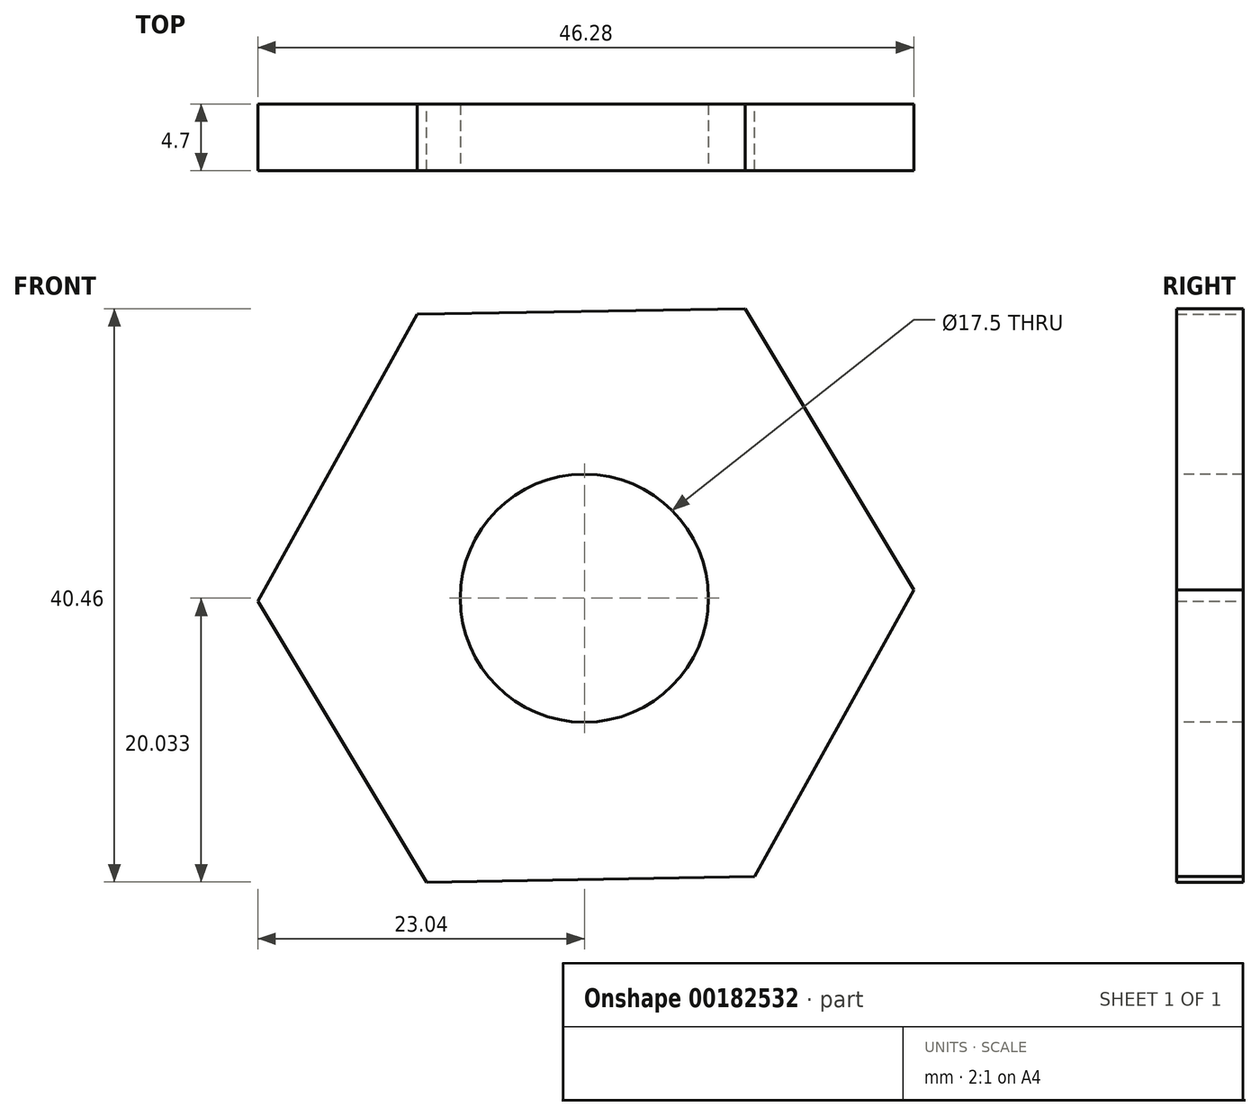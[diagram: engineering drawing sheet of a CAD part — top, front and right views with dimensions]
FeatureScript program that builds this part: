
annotation { "Feature Type Name" : "Feature", "Feature Type Description" : "" }
export const myFeature = defineFeature(function(context is Context, id is Id, definition is map)
    precondition{}
    {
        {
            var Q0;
            Q0=qCreatedBy(makeId("Front.planeOp"),FACE);
            var sketch = newSketch(context, id + "F0", { "sketchPlane" : qUnion([Q0])});
            skCircle(sketch, "E0.cCircle", {"center": v(-18.76, 37.82) * mm, "radius": 23.14 * mm, "construction": true});
            skLineSegment(sketch, "E0.0", {"start": v(4.38, 38.2) * mm, "end": v(-6.85, 17.97) * mm});
            skLineSegment(sketch, "E0.1", {"start": v(-6.85, 17.97) * mm, "end": v(-30, 17.59) * mm});
            skLineSegment(sketch, "E0.2", {"start": v(-30, 17.59) * mm, "end": v(-41.9, 37.43) * mm});
            skLineSegment(sketch, "E0.3", {"start": v(-41.9, 37.43) * mm, "end": v(-30.66, 57.66) * mm});
            skLineSegment(sketch, "E0.4", {"start": v(-30.66, 57.66) * mm, "end": v(-7.53, 58.05) * mm});
            skLineSegment(sketch, "E0.5", {"start": v(-7.53, 58.05) * mm, "end": v(4.38, 38.2) * mm});
            skSolve(sketch);
        }
        {
            var Q0;
            Q0=makeQuery(id+"F0.imprint","IMPRINT",FACE,{"disambiguationData":[TD([[makeQuery(id+"F0.imprint","IMPRINT",EDGE,{"derivedFrom":sQuery(id+"F0.wireOp",EDGE,"E0.0")}),-1.0]])]});
            extrude(context, id + "F1", {"entities" : qUnion([Q0]), "depth" : 4.7 * mm});
        }
        {
            var Q0;
            Q0=makeQuery(id+"F1.opExtrude","CAP_FACE",FACE,{"disambiguationData":[OSD([sQuery(id+"F0.wireOp",EDGE,"E0.0"),sQuery(id+"F0.wireOp",EDGE,"E0.1"),sQuery(id+"F0.wireOp",EDGE,"E0.2"),sQuery(id+"F0.wireOp",EDGE,"E0.3"),sQuery(id+"F0.wireOp",EDGE,"E0.4"),sQuery(id+"F0.wireOp",EDGE,"E0.5")])],"isStart":false});
            var sketch = newSketch(context, id + "F2", { "sketchPlane" : qUnion([Q0])});
            skCircle(sketch, "E1", {"center": v(-18.86, 37.62) * mm, "radius": 8.75 * mm});
            skSolve(sketch);
        }
        {
            var Q0;
            Q0=makeQuery(id+"F2.imprint","IMPRINT",FACE,{"disambiguationData":[TD([[makeQuery(id+"F2.imprint","IMPRINT",EDGE,{"derivedFrom":sQuery(id+"F2.wireOp",EDGE,"E1")}),1.0]])]});
            extrude(context, id + "F3", {"entities" : qUnion([Q0]), "operationType" : NewBodyOperationType.REMOVE, "oppositeDirection" : true, "depth" : 50.8 * mm});
        }
    });
